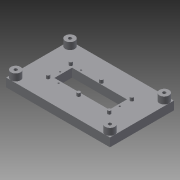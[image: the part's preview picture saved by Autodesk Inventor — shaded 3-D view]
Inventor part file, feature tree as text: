
AUTODESK INVENTOR PART (.ipt)
format: ipt  version: 2015 (Build 190159000, 159)  size: 169,472 bytes
history: native  units: in
note: dims shown in document units (in); Inventor stores cm internally (conversion verified against a paired STEP export)
features: extrude x4, sketch x2
ambient origin geometry x8: Origin, YZ Plane, XZ Plane, XY Plane, X Axis, Y Axis, Z Axis, Center Point
bodies: Solid1 (feature_tree)
feature tree (6):
  extrude  "Extrusion1"  Depth=2.5591in
  extrude  "Extrusion2"  Depth=0.0394in
  extrude  "Extrusion4"  Depth=0.0906in
  extrude  "Extrusion5"  Depth=0.0906in
  sketch  "Sketch1"  dims[d0=1.5748in d1=2.5591in]
  sketch  "Sketch5"  dims[d2=0.2091in d3=0.0in d4=0.0394in d15=0.5535in d23=1.4701in d31=0.1181in d32=0.0in d39=0.2217in d59=0.0787in d60=0.0in d69=0.1181in d70=0.1181in d79=0.0787in d82=0.0394in d83=0.0394in d84=0.0394in d85=0.0394in d90=0.1181in d91=0.1181in d92=0.0787in d93=1.3386in d94=2.3228in d95=0.0787in d96=0.0787in d97=0.0787in d98=0.0906in d99=0.0in]
